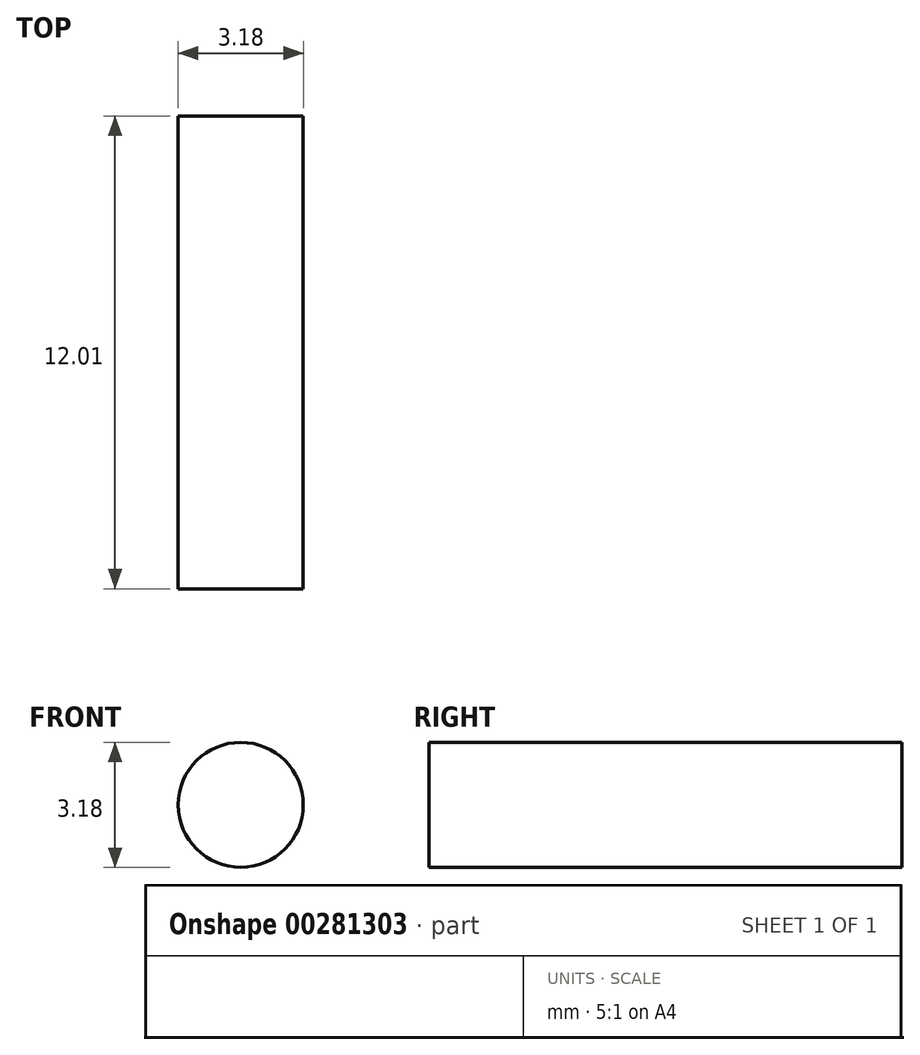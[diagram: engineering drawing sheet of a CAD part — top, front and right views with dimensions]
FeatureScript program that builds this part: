
annotation { "Feature Type Name" : "Feature", "Feature Type Description" : "" }
export const myFeature = defineFeature(function(context is Context, id is Id, definition is map)
    precondition{}
    {
        {
            var Q0;
            Q0=qCreatedBy(makeId("Front.planeOp"),FACE);
            var sketch = newSketch(context, id + "F0", { "sketchPlane" : qUnion([Q0])});
            skCircle(sketch, "E0", {"center": v(0, 0) * mm, "radius": 1.59 * mm});
            skSolve(sketch);
        }
        {
            var Q0;
            Q0 = qSketchRegion(id + "F0", true);
            extrude(context, id + "F1", {"entities" : qUnion([Q0]), "depth" : 12 * mm});
        }
    });
